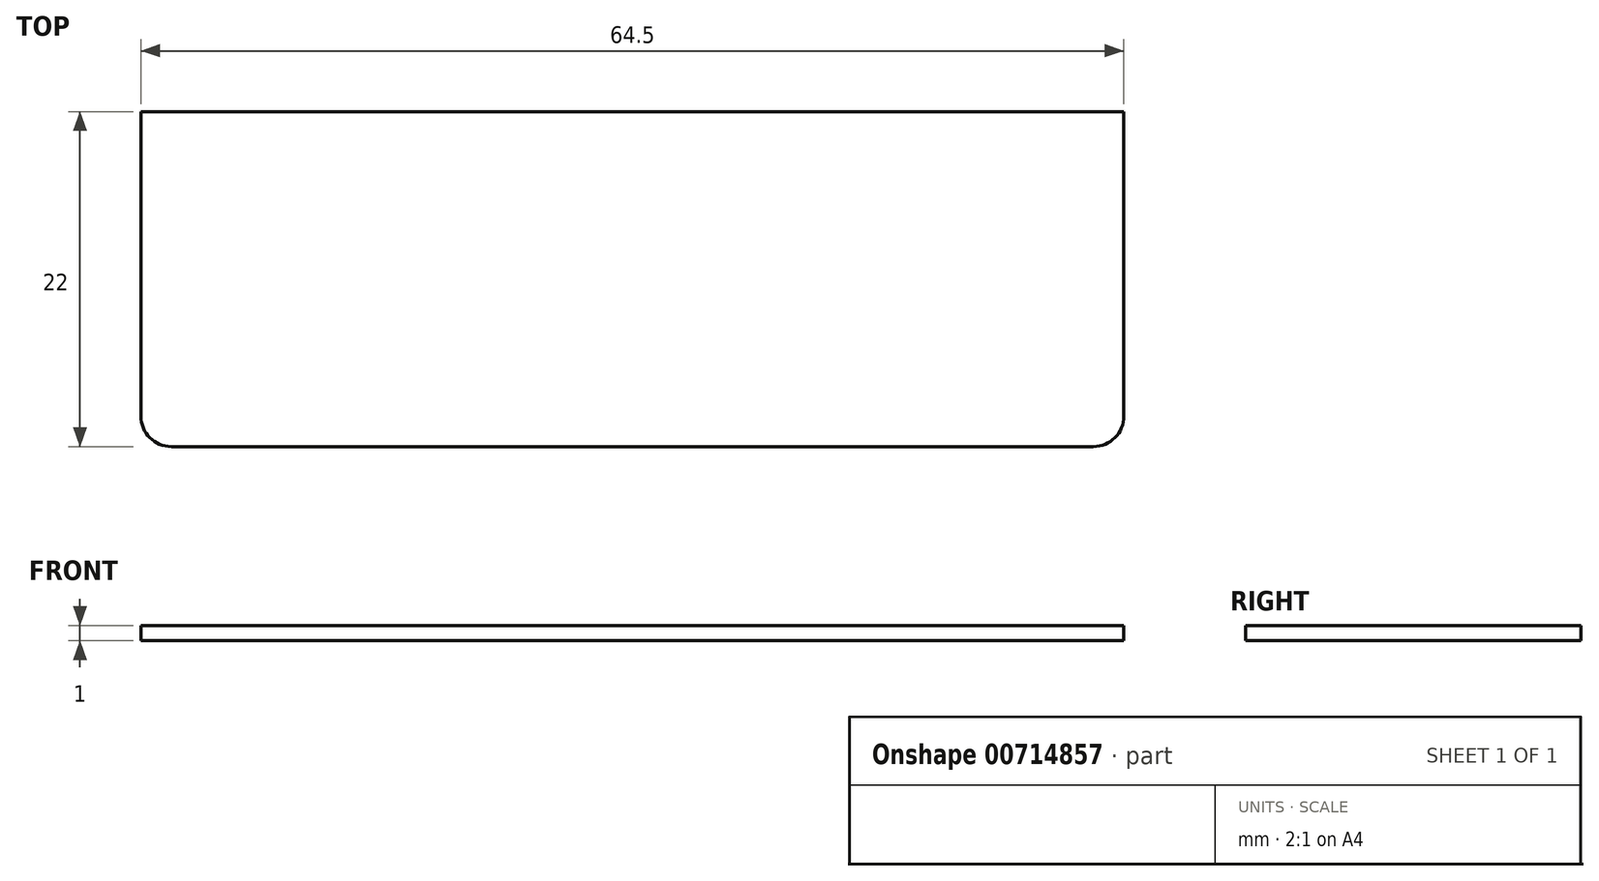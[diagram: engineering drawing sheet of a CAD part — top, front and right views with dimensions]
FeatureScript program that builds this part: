
annotation { "Feature Type Name" : "Feature", "Feature Type Description" : "" }
export const myFeature = defineFeature(function(context is Context, id is Id, definition is map)
    precondition{}
    {
        {
            var Q0;
            Q0=qCreatedBy(makeId("Top.planeOp"),FACE);
            var sketch = newSketch(context, id + "F0", { "sketchPlane" : qUnion([Q0])});
            skLineSegment(sketch, "E0.bottom", {"start": v(-32.4, 11.16) * mm, "end": v(32.1, 11.16) * mm});
            skLineSegment(sketch, "E0.top", {"start": v(-32.4, -10.84) * mm, "end": v(32.1, -10.84) * mm});
            skLineSegment(sketch, "E0.left", {"start": v(-32.4, 11.16) * mm, "end": v(-32.4, -10.84) * mm});
            skLineSegment(sketch, "E0.right", {"start": v(32.1, 11.16) * mm, "end": v(32.1, -10.84) * mm});
            skSolve(sketch);
        }
        {
            var Q0;
            Q0=qSketchRegion(id+"F0",true);
            extrude(context, id + "F1", {"entities" : qUnion([Q0]), "depth" : 1 * mm, "offsetDistance" : 25 * mm});
        }
        {
            var Q0;
            Q0=makeQuery(id+"F1.opExtrude","SWEPT_EDGE",EDGE,{"disambiguationData":[OSD([sQuery(id+"F0.wireOp",EDGE,"E0.top"),sQuery(id+"F0.wireOp",EDGE,"E0.left")])]});
            var Q1;
            Q1=makeQuery(id+"F1.opExtrude","SWEPT_EDGE",EDGE,{"disambiguationData":[OSD([sQuery(id+"F0.wireOp",EDGE,"E0.top"),sQuery(id+"F0.wireOp",EDGE,"E0.right")])]});
            fillet(context, id + "F2", {"entities" : qUnion([Q0, Q1]), "radius" : 2 * mm, "tangentPropagation" : true, "allowEdgeOverflow" : false});
        }
    });
